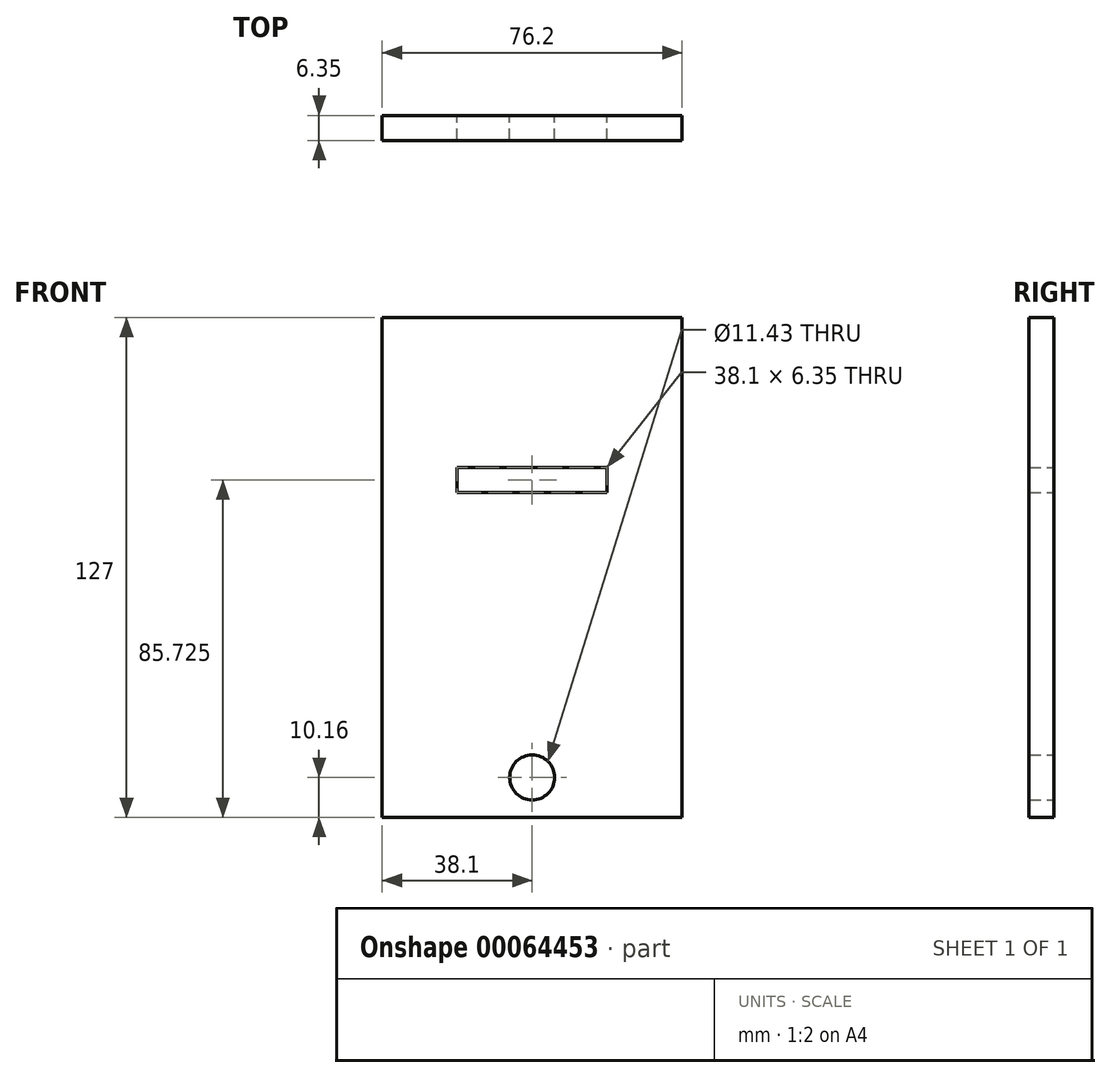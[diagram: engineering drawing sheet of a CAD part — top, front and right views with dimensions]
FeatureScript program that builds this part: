
annotation { "Feature Type Name" : "Feature", "Feature Type Description" : "" }
export const myFeature = defineFeature(function(context is Context, id is Id, definition is map)
    precondition{}
    {
        {
            var Q0;
            Q0=qCreatedBy(makeId("Front.planeOp"),FACE);
            var sketch = newSketch(context, id + "F0", { "sketchPlane" : qUnion([Q0])});
            skLineSegment(sketch, "E0.rect.bottom", {"start": v(38.1, 63.5) * mm, "end": v(-38.1, 63.5) * mm});
            skLineSegment(sketch, "E0.rect.top", {"start": v(38.1, -63.5) * mm, "end": v(-38.1, -63.5) * mm});
            skLineSegment(sketch, "E0.rect.left", {"start": v(38.1, 63.5) * mm, "end": v(38.1, -63.5) * mm});
            skLineSegment(sketch, "E0.rect.right", {"start": v(-38.1, 63.5) * mm, "end": v(-38.1, -63.5) * mm});
            skPoint(sketch, "E0.rect.middle", {"position": v(0, 0) * mm});
            skLineSegment(sketch, "E1.bottom", {"start": v(-19.05, 25.4) * mm, "end": v(19.05, 25.4) * mm});
            skLineSegment(sketch, "E1.top", {"start": v(-19.05, 19.05) * mm, "end": v(19.05, 19.05) * mm});
            skLineSegment(sketch, "E1.left", {"start": v(-19.05, 25.4) * mm, "end": v(-19.05, 19.05) * mm});
            skLineSegment(sketch, "E1.right", {"start": v(19.05, 25.4) * mm, "end": v(19.05, 19.05) * mm});
            skPoint(sketch, "E2", {"position": v(0, 25.4) * mm});
            skPoint(sketch, "E3", {"position": v(0, 63.5) * mm});
            skPoint(sketch, "E4", {"position": v(126.35, 25.78) * mm});
            skLineSegment(sketch, "E5", {"start": v(0, 63.5) * mm, "end": v(0, 25.4) * mm, "construction": true});
            skCircle(sketch, "E6", {"center": v(0, -53.34) * mm, "radius": 5.72 * mm});
            skPoint(sketch, "E7", {"position": v(0, -63.5) * mm});
            skLineSegment(sketch, "E8", {"start": v(0, -53.34) * mm, "end": v(0, -63.5) * mm, "construction": true});
            skSolve(sketch);
        }
        {
            var Q0;
            Q0 = qSketchRegion(id + "F0", true);
            extrude(context, id + "F1", {"entities" : qUnion([Q0]), "depth" : 6.35 * mm});
        }
    });
